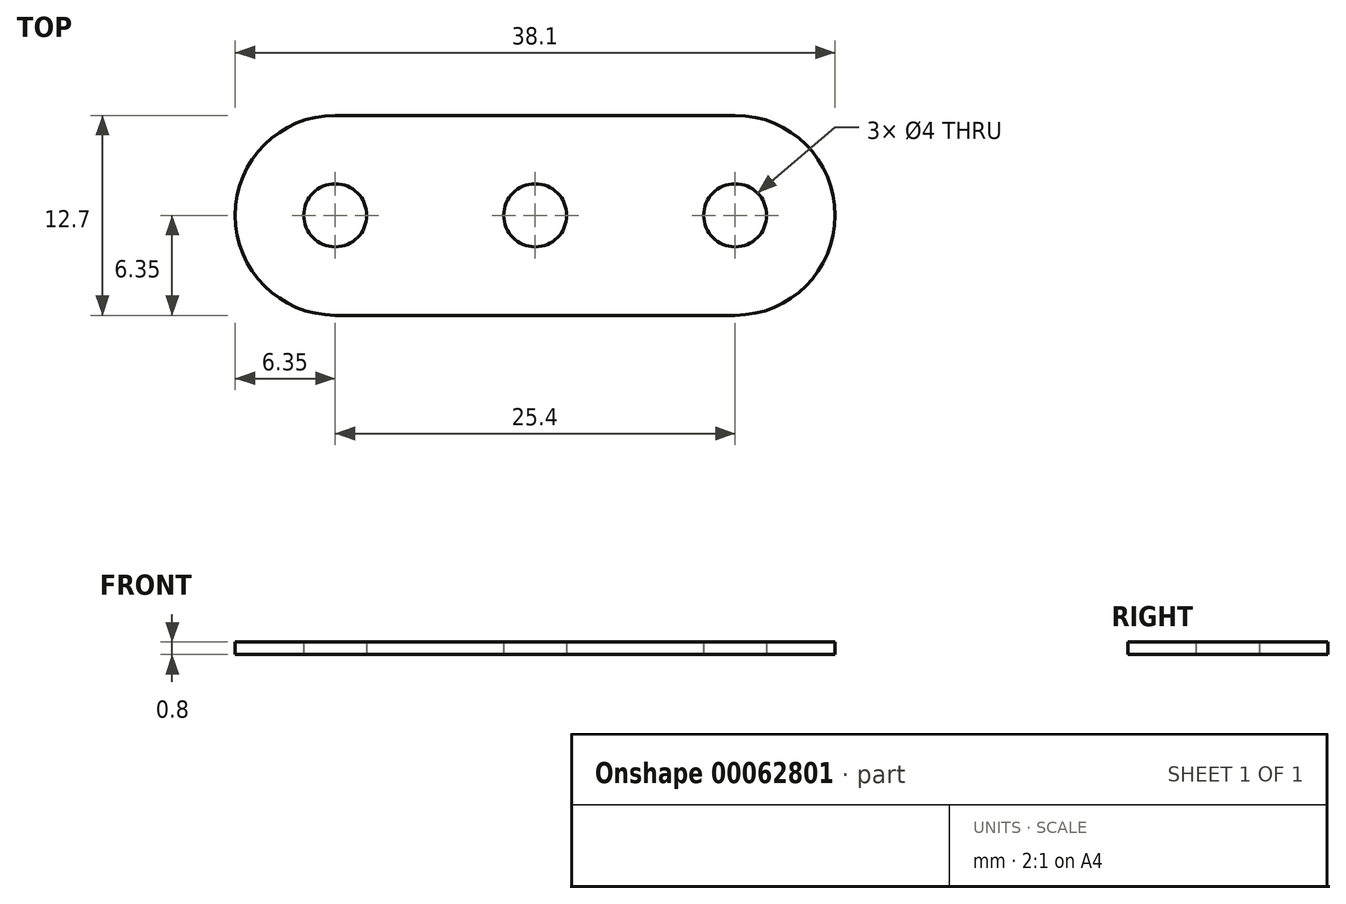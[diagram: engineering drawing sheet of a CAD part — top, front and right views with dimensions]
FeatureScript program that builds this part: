
annotation { "Feature Type Name" : "Feature", "Feature Type Description" : "" }
export const myFeature = defineFeature(function(context is Context, id is Id, definition is map)
    precondition{}
    {
        {
            var Q0;
            Q0=qCreatedBy(makeId("Top.planeOp"),FACE);
            var sketch = newSketch(context, id + "F0", { "sketchPlane" : qUnion([Q0])});
            skCircle(sketch, "E0", {"center": v(0, 0) * mm, "radius": 2 * mm});
            skCircle(sketch, "E1.1.0.0", {"center": v(12.7, 0) * mm, "radius": 2 * mm});
            skCircle(sketch, "E1.2.0.0", {"center": v(25.4, 0) * mm, "radius": 2 * mm});
            skLineSegment(sketch, "E1.direction1", {"start": v(0, 0) * mm, "end": v(12.7, 0) * mm, "construction": true});
            skLineSegment(sketch, "E2.rect.bottom", {"start": v(25.4, -6.35) * mm, "end": v(0, -6.35) * mm});
            skLineSegment(sketch, "E2.rect.top", {"start": v(25.4, 6.35) * mm, "end": v(0, 6.35) * mm});
            skLineSegment(sketch, "E2.rect.left", {"start": v(31.75, 0) * mm, "end": v(31.75, 0) * mm});
            skLineSegment(sketch, "E2.rect.right", {"start": v(-6.35, 0) * mm, "end": v(-6.35, 0) * mm});
            skPoint(sketch, "E3.visualSharp", {"position": v(-6.35, 6.35) * mm});
            skArc(sketch, "E3.filletArc", {"start": v(0, 6.35) * mm, "mid": v(-4.5, 4.5) * mm, "end": v(-6.35, 0) * mm});
            skPoint(sketch, "E4.visualSharp", {"position": v(-6.35, -6.35) * mm});
            skArc(sketch, "E4.filletArc", {"start": v(-6.35, 0) * mm, "mid": v(-4.5, -4.5) * mm, "end": v(0, -6.35) * mm});
            skPoint(sketch, "E5.visualSharp", {"position": v(31.75, 6.35) * mm});
            skArc(sketch, "E5.filletArc", {"start": v(31.75, 0) * mm, "mid": v(29.9, 4.5) * mm, "end": v(25.4, 6.35) * mm});
            skPoint(sketch, "E6.visualSharp", {"position": v(31.75, -6.35) * mm});
            skArc(sketch, "E6.filletArc", {"start": v(25.4, -6.35) * mm, "mid": v(29.9, -4.5) * mm, "end": v(31.75, 0) * mm});
            skSolve(sketch);
        }
        {
            var Q0;
            Q0=makeQuery(id+"F0.imprint","IMPRINT",FACE,{"disambiguationData":[TD([[makeQuery(id+"F0.imprint","IMPRINT",EDGE,{"derivedFrom":sQuery(id+"F0.wireOp",EDGE,"E0")}),-1.0]])]});
            extrude(context, id + "F1", {"entities" : qUnion([Q0]), "depth" : 0.8 * mm});
        }
    });
